# Revit family: KEUCO_14910005200
name_source: partatom
category: Allgemeines Modell
revit_build: Autodesk Revit 2016 (Build: 20150220_1215(x64)
units: mm (PartAtom-declared; Revit-internal decimal feet)

## family parameters
Arbeitsebenenbasiert = Ja
Beim Laden mit Abzugskörper schneiden = Nein
Bemaßung runder Anschluss = Durchmesser verwenden
Gemeinsam genutzt = Nein
Immer vertikal = Nein
Kann Basisbauteil für Bewehrung sein = Nein
Raumberechnungspunkt = Nein
Teiletyp = Normal

## types (3) — shared parameters
Hersteller = KEUCO
Kategorie = ACC
Material Regal = Hochwertige Cristallinglas-Platte
Rahmen Material = Verchromt
Serie = Plan
URL = https://www.keuco.com
Verwendung = GWC / WP
Vorgabe-Ansicht = 1219 mm

## per-type parameters (varying)
| type | Ausschreibungstext | Gewicht | Länge | Tiefe |
| 14910005200 | KEUCO PLAN Glasplatte 14910005200 
Hochwertige Cristallinglas-Platte, 
ohne Grünkante, Unterseite mattiert 
passend zur Ablagekonsole Artikel-Nr. 14910 
Breite 220 mm, Tiefe 100 mm, Stärke 8 mm 
Die maximale Ausladung inklusive Ablagekonsole beträgt 110 mm 
Die Ablagekonsole ist separat zu bestellen! | 0.522 | 220 mm  [stored 0.721785 ft] | 100 mm  [stored 0.328084 ft] |
| 14910005300 | KEUCO PLAN Glasplatte 14910005300 
Hochwertige Cristallinglas-Platte, 
ohne Grünkante, Unterseite mattiert 
passend zur Ablagekonsole Artikel-Nr. 14910 
Breite 350 mm, Tiefe 120 mm, Stärke 8 mm 
Die maximale Ausladung inklusive Ablagekonsole beträgt 130 mm 
Die Ablagekonsole ist separat zu bestellen! | 0.974 | 350 mm  [stored 1.14829 ft] | 120 mm  [stored 0.393701 ft] |
| 14910005500 | KEUCO PLAN Glasplatte 14910005500 
Hochwertige Cristallinglas-Platte, 
ohne Grünkante, Unterseite mattiert 
passend zur Ablagekonsole Artikel-Nr. 14910 
Breite 550 mm, Tiefe 120 mm, Stärke 8 mm 
Die maximale Ausladung inklusive Ablagekonsole beträgt 130 mm 
Die Ablagekonsole ist separat zu bestellen! | 1.46 | 500 mm  [stored 1.64042 ft] | 120 mm  [stored 0.393701 ft] |

note: column(s) folded — value = type name in every type: Artikelnummer

note: [stored X ft] marks values corroborated as IEEE doubles in the binary element streams (Revit-internal decimal feet)

## geometry (parser evidence)
native form markers: Blend x2, Sweep x3
no freeform markers — native parametric forms only
